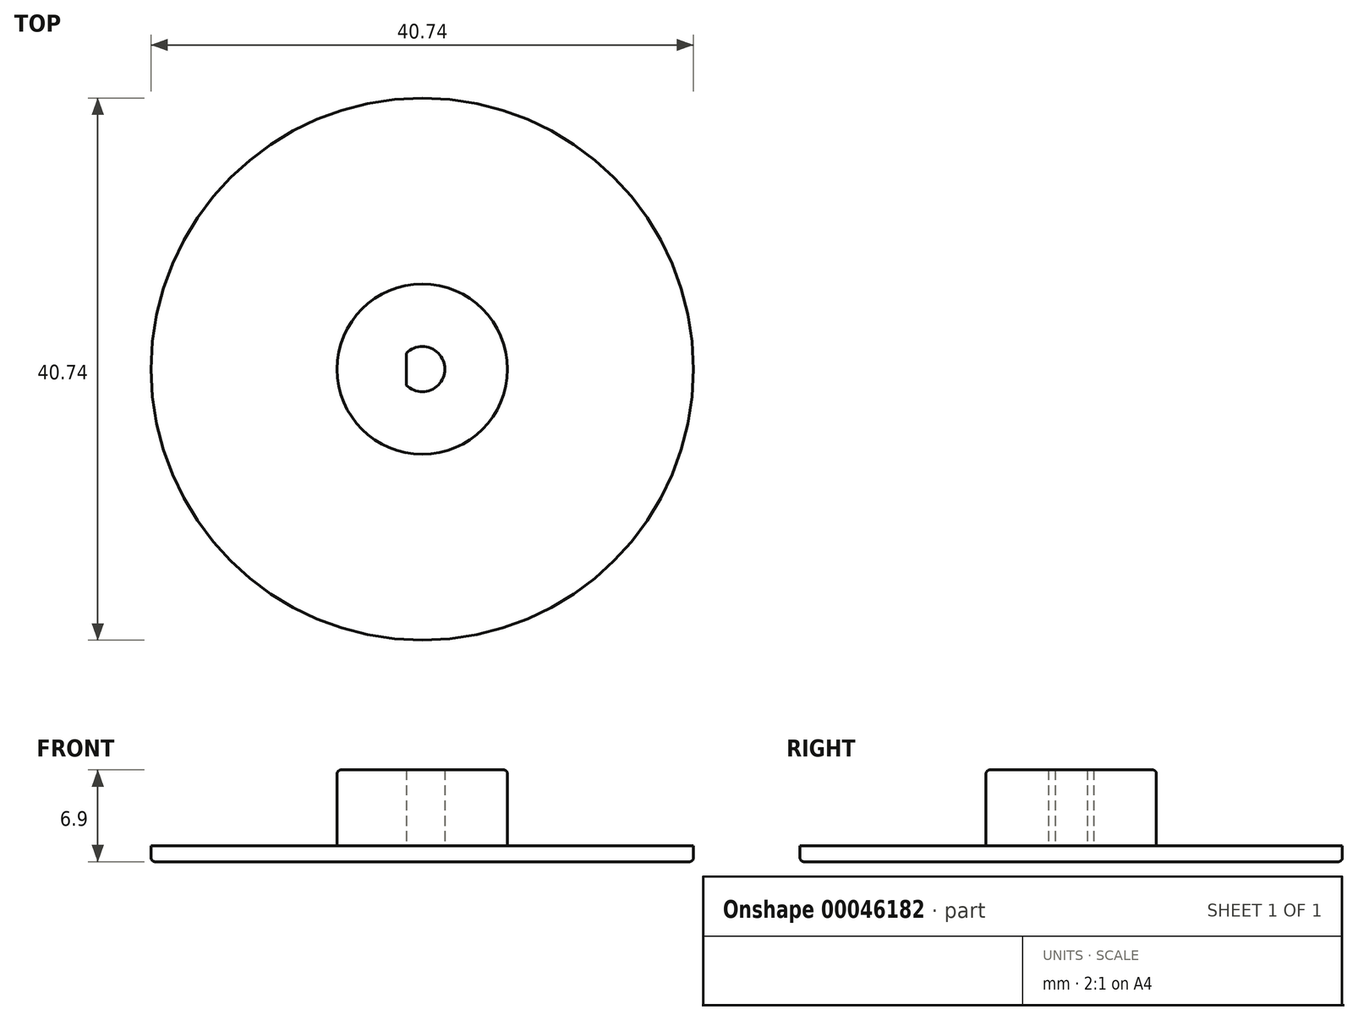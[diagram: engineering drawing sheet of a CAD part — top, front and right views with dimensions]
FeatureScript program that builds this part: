
annotation { "Feature Type Name" : "Feature", "Feature Type Description" : "" }
export const myFeature = defineFeature(function(context is Context, id is Id, definition is map)
    precondition{}
    {
        {
            var Q0;
            Q0=qCreatedBy(makeId("Top.planeOp"),FACE);
            var sketch = newSketch(context, id + "F0", { "sketchPlane" : qUnion([Q0])});
            skCircle(sketch, "E0", {"center": v(0, 0) * mm, "radius": 20.37 * mm});
            skLineSegment(sketch, "E1", {"start": v(0, 0) * mm, "end": v(0, 20.37) * mm, "construction": true});
            skCircle(sketch, "E2.0", {"center": v(0, 0) * mm, "radius": 6.4 * mm});
            skArc(sketch, "E3", {"start": v(-1, -1.12) * mm, "mid": v(1.5, 0) * mm, "end": v(-1, 1.12) * mm, "construction": true});
            skLineSegment(sketch, "E4", {"start": v(-1, 1.12) * mm, "end": v(-1, -1.12) * mm, "construction": true});
            skArc(sketch, "E5.0", {"start": v(-1.2, -1.2) * mm, "mid": v(1.7, 0) * mm, "end": v(-1.2, 1.2) * mm});
            skLineSegment(sketch, "E5.1", {"start": v(-1.2, 1.2) * mm, "end": v(-1.2, -1.2) * mm});
            skSolve(sketch);
        }
        {
            var Q0;
            Q0=makeQuery(id+"F0.imprint","IMPRINT",FACE,{"disambiguationData":[TD([[makeQuery(id+"F0.imprint","IMPRINT",EDGE,{"derivedFrom":sQuery(id+"F0.wireOp",EDGE,"E2.0")}),1.0]])]});
            var Q1;
            Q1=makeQuery(id+"F0.imprint","IMPRINT",FACE,{"disambiguationData":[TD([[makeQuery(id+"F0.imprint","IMPRINT",EDGE,{"derivedFrom":sQuery(id+"F0.wireOp",EDGE,"E0")}),1.0]])]});
            var Q2;
            Q2=makeQuery(id+"F0.imprint","IMPRINT",FACE,{"disambiguationData":[TD([[makeQuery(id+"F0.imprint","IMPRINT",EDGE,{"derivedFrom":sQuery(id+"F0.wireOp",EDGE,"E5.0")}),1.0]])]});
            extrude(context, id + "F1", {"entities" : qUnion([Q0, Q1, Q2]), "oppositeDirection" : true, "depth" : 1.2 * mm});
        }
        {
            var Q0;
            Q0=makeQuery(id+"F0.imprint","IMPRINT",FACE,{"disambiguationData":[TD([[makeQuery(id+"F0.imprint","IMPRINT",EDGE,{"derivedFrom":sQuery(id+"F0.wireOp",EDGE,"E2.0")}),1.0]])]});
            extrude(context, id + "F2", {"entities" : qUnion([Q0]), "operationType" : NewBodyOperationType.ADD, "depth" : 5.7 * mm});
        }
        {
            var Q0;
            Q0=makeQuery(id+"F1.opExtrude","CAP_EDGE",EDGE,{"disambiguationData":[OSD([sQuery(id+"F0.wireOp",EDGE,"E0")])],"isStart":false});
            var Q1;
            Q1=makeQuery(id+"F2.opExtrude","CAP_EDGE",EDGE,{"disambiguationData":[OSD([sQuery(id+"F0.wireOp",EDGE,"E2.0")])],"isStart":false});
            fillet(context, id + "F3", {"entities" : qUnion([Q0, Q1]), "radius" : .3 * mm, "tangentPropagation" : true, "allowEdgeOverflow" : false});
        }
    });
